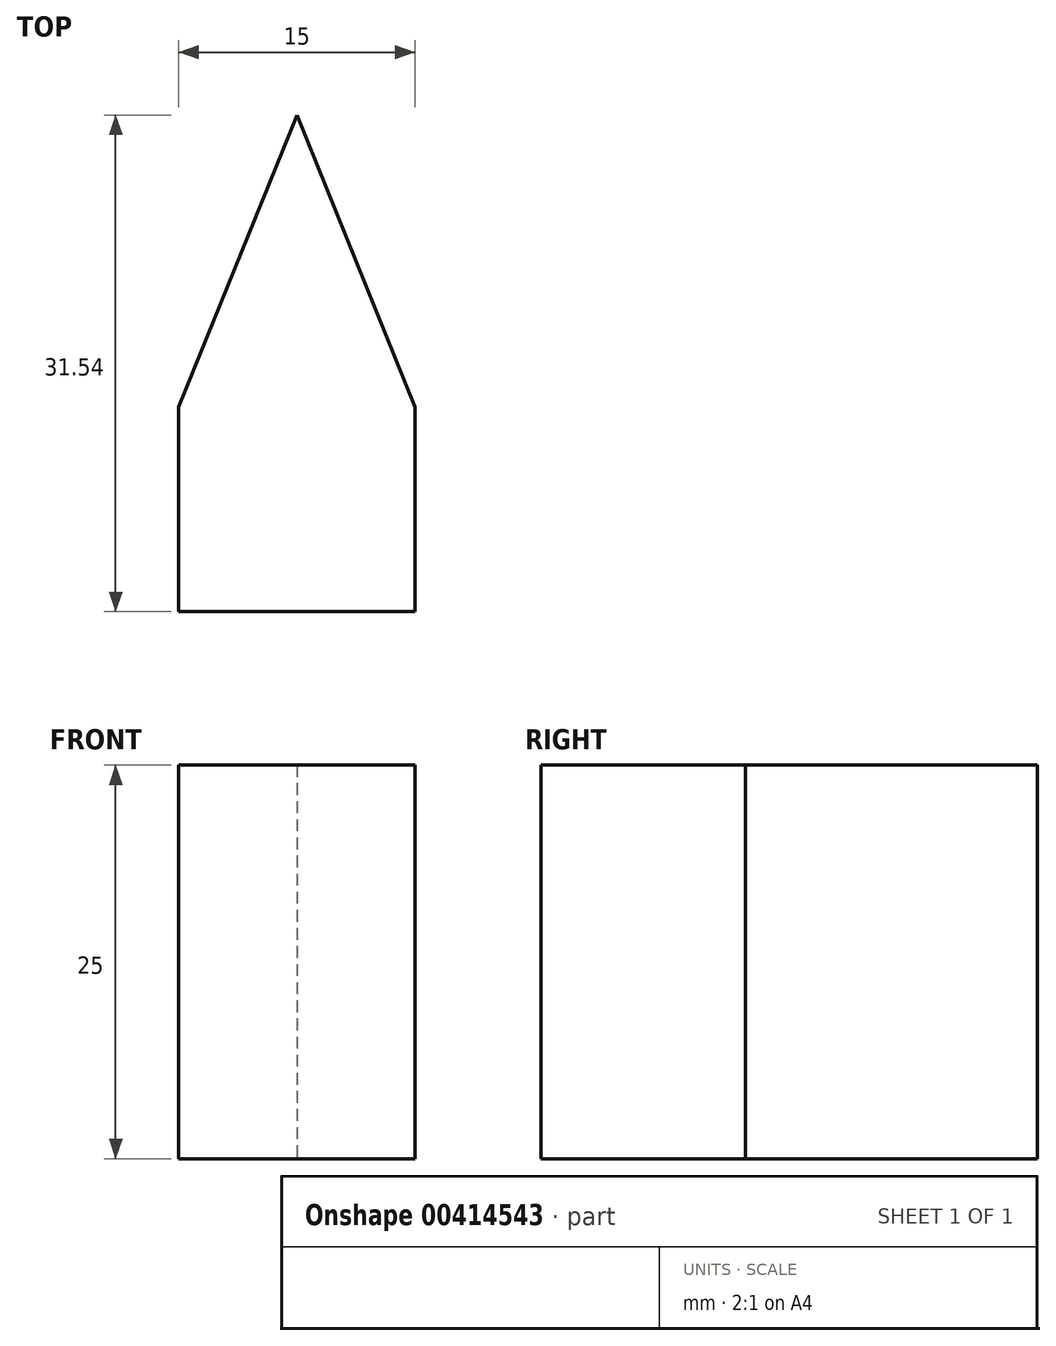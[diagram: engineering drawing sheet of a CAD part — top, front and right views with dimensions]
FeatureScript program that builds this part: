
annotation { "Feature Type Name" : "Feature", "Feature Type Description" : "" }
export const myFeature = defineFeature(function(context is Context, id is Id, definition is map)
    precondition{}
    {
        {
            var Q0;
            Q0=qCreatedBy(makeId("Top.planeOp"),FACE);
            var sketch = newSketch(context, id + "F0", { "sketchPlane" : qUnion([Q0])});
            skLineSegment(sketch, "E0.bottom", {"start": v(-12.64, 10.63) * mm, "end": v(2.36, 10.63) * mm});
            skLineSegment(sketch, "E0.top", {"start": v(-12.64, 23.63) * mm, "end": v(2.36, 23.63) * mm});
            skLineSegment(sketch, "E0.left", {"start": v(-12.64, 10.63) * mm, "end": v(-12.64, 23.63) * mm});
            skLineSegment(sketch, "E0.right", {"start": v(2.36, 10.63) * mm, "end": v(2.36, 23.63) * mm});
            skLineSegment(sketch, "E1", {"start": v(-12.64, 23.63) * mm, "end": v(-5.14, 42.17) * mm});
            skLineSegment(sketch, "E2", {"start": v(-5.14, 42.17) * mm, "end": v(2.36, 23.63) * mm});
            skSolve(sketch);
        }
        {
            var Q0;
            Q0=makeQuery(id+"F0.imprint","IMPRINT",FACE,{"disambiguationData":[TD([[makeQuery(id+"F0.imprint","IMPRINT",EDGE,{"derivedFrom":sQuery(id+"F0.wireOp",EDGE,"E0.bottom")}),1.0]])]});
            var Q1;
            Q1=makeQuery(id+"F0.imprint","IMPRINT",FACE,{"disambiguationData":[TD([[makeQuery(id+"F0.imprint","IMPRINT",EDGE,{"derivedFrom":sQuery(id+"F0.wireOp",EDGE,"E0.top")}),1.0]])]});
            extrude(context, id + "F1", {"entities" : qUnion([Q0, Q1]), "depth" : 25 * mm});
        }
    });
